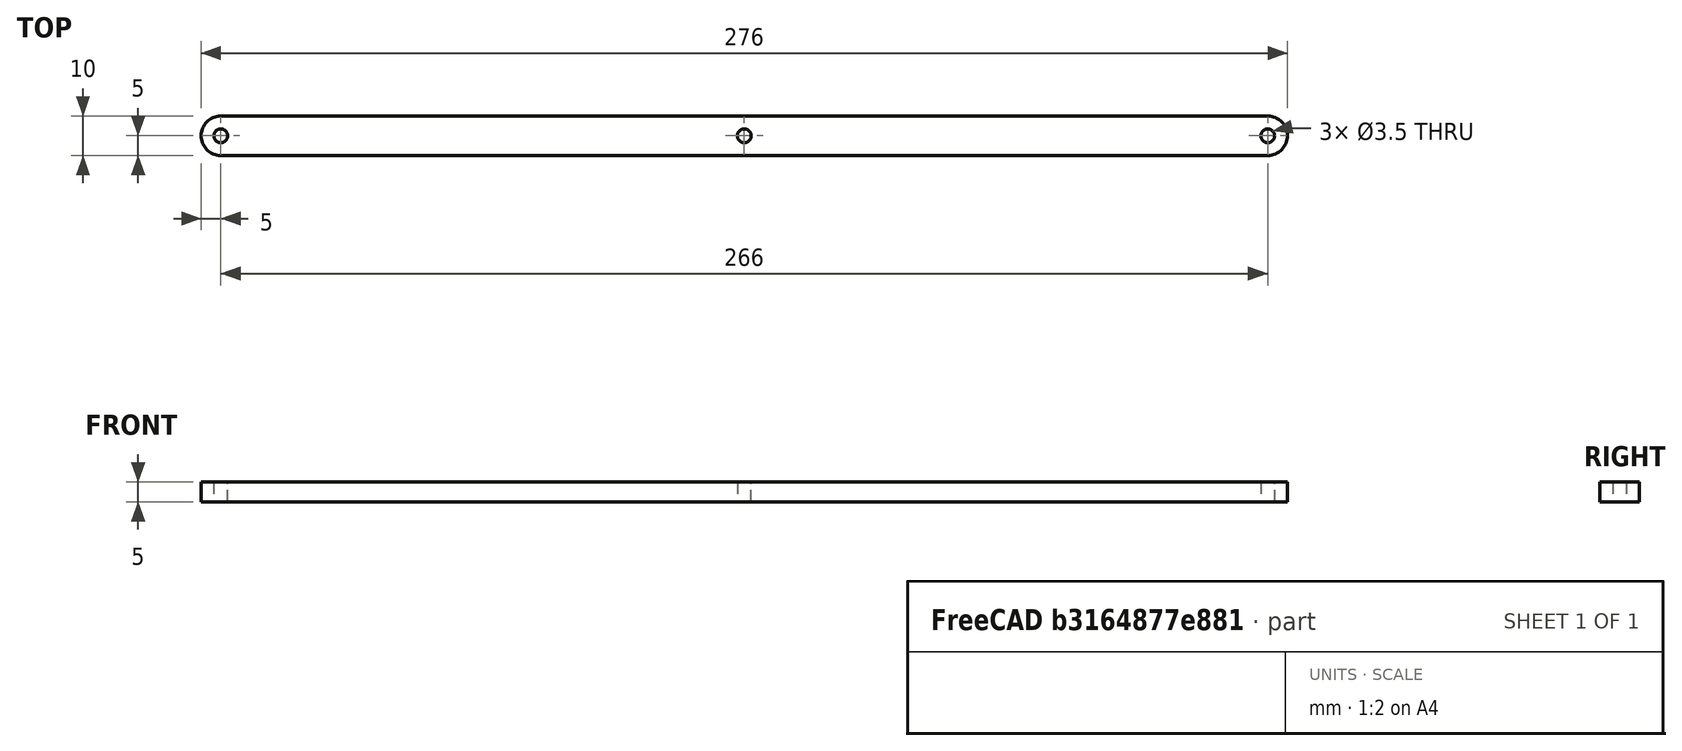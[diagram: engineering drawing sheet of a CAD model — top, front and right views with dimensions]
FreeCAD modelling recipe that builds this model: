
FCSTD DOCUMENT  (FreeCAD 0.20R29410 (Git))
Label: brace
License: All rights reserved
LicenseURL: http://en.wikipedia.org/wiki/All_rights_reserved
objects: Sketcher::SketchObject×1, PartDesign::Pad×1, PartDesign::Body×1, PartDesign::CoordinateSystem×1, App::Part×1
note: 5 computed .brp shape members not serialized (recipe doc carries the construction recipe); baked Part::Feature solids carry a one-line shape summary decoded from their .brp

FEATURE [Sketcher::SketchObject] Sketch
  FullyConstrained = true
  MapMode = 5
  Support = -> [XY_Plane]
  expr: Constraints[11] = <<planB>>#<<data>>.clearance_m3
  sketch-geometry (7):
    g0: ArcOfCircle CenterX=0 CenterY=0 CenterZ=0 NormalX=0 NormalY=0 NormalZ=1 AngleXU=0 Radius=5 StartAngle=1.5708 EndAngle=4.71239
    g1: ArcOfCircle CenterX=266 CenterY=0 CenterZ=0 NormalX=0 NormalY=0 NormalZ=1 AngleXU=0 Radius=5 StartAngle=4.71239 EndAngle=7.85398
    g2: LineSegment StartX=-9e-16 StartY=-5 StartZ=0 EndX=266 EndY=-5 EndZ=0
    g3: LineSegment StartX=266 StartY=5 StartZ=0 EndX=0 EndY=5 EndZ=0
    g4: Circle CenterX=0 CenterY=0 CenterZ=0 NormalX=0 NormalY=0 NormalZ=1 AngleXU=0 Radius=1.75
    g5: Circle CenterX=266 CenterY=0 CenterZ=0 NormalX=0 NormalY=0 NormalZ=1 AngleXU=0 Radius=1.75
    g6: Circle CenterX=133 CenterY=0 CenterZ=0 NormalX=0 NormalY=0 NormalZ=1 AngleXU=0 Radius=1.75
  constraints (15):
    c: Tangent(g0,g2) = -1.5708
    c: Tangent(g2,g1) = -1.5708
    c: Tangent(g1,g3) = -1.5708
    c: Tangent(g3,g0) = -1.5708
    c: Equal(g0,g1)
    c: Coincident(g0,g-1)
    c: Horizontal(g2)
    c: Coincident(g4,g0)
    c: Coincident(g5,g1)
    c: Equal(g5,g6)
    c: Equal(g6,g4)
    c: Diameter(g4) = 3.5
    c: Symmetric(g0,g1,g6)
    c: Distance(g3) = 266
    c: Diameter(g0) = 10
FEATURE [PartDesign::Pad] Pad
  Direction = (0,0,1)
  Length = 5
  Length2 = 10
  Profile = -> Sketch
  ReferenceAxis = -> Sketch [N_Axis]
  Type = 0
FEATURE [PartDesign::Body] Body
  Group = -> [Sketch,Pad]
  Origin = -> Origin
  Tip = -> Pad
FEATURE [PartDesign::CoordinateSystem] LCS_0
  AttacherType = Attacher::AttachEngine3D
  MapMode = 2
  Support = -> [X_Axis001]
FEATURE [App::Part] brace
  Group = -> [LCS_0,Body]
  Origin = -> Origin001
